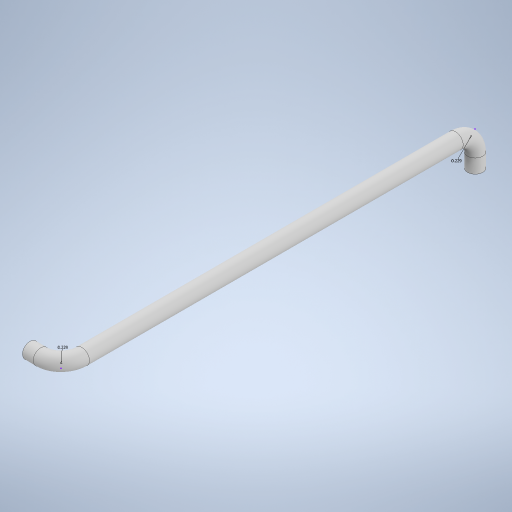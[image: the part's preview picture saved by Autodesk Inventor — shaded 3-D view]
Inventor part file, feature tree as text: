
AUTODESK INVENTOR PART (.ipt)
format: ipt  version: 2023 (Build 270158000, 158)  size: 1,708,032 bytes
history: native  units: in
note: dims shown in document units (in); Inventor stores cm internally (conversion verified against a paired STEP export)
features: other x2, sketch x2, plane x1, sweep x1
ambient origin geometry x8: Origin, YZ Plane, XZ Plane, XY Plane, X Axis, Y Axis, Z Axis, Center Point
bodies: Solid1 (feature_tree)
feature tree (6):
  other  "s282_locomotive_body"
  sketch  "3D Sketch1"
  plane  "Work Plane1"
  sweep  "Sweep1"
  sketch  "Sketch1"  dims[d0=0.0in d1=0.0in d2=7.0in d6=9.0in d7=9.0in]
  other  "s282_locomotive_body_0"
